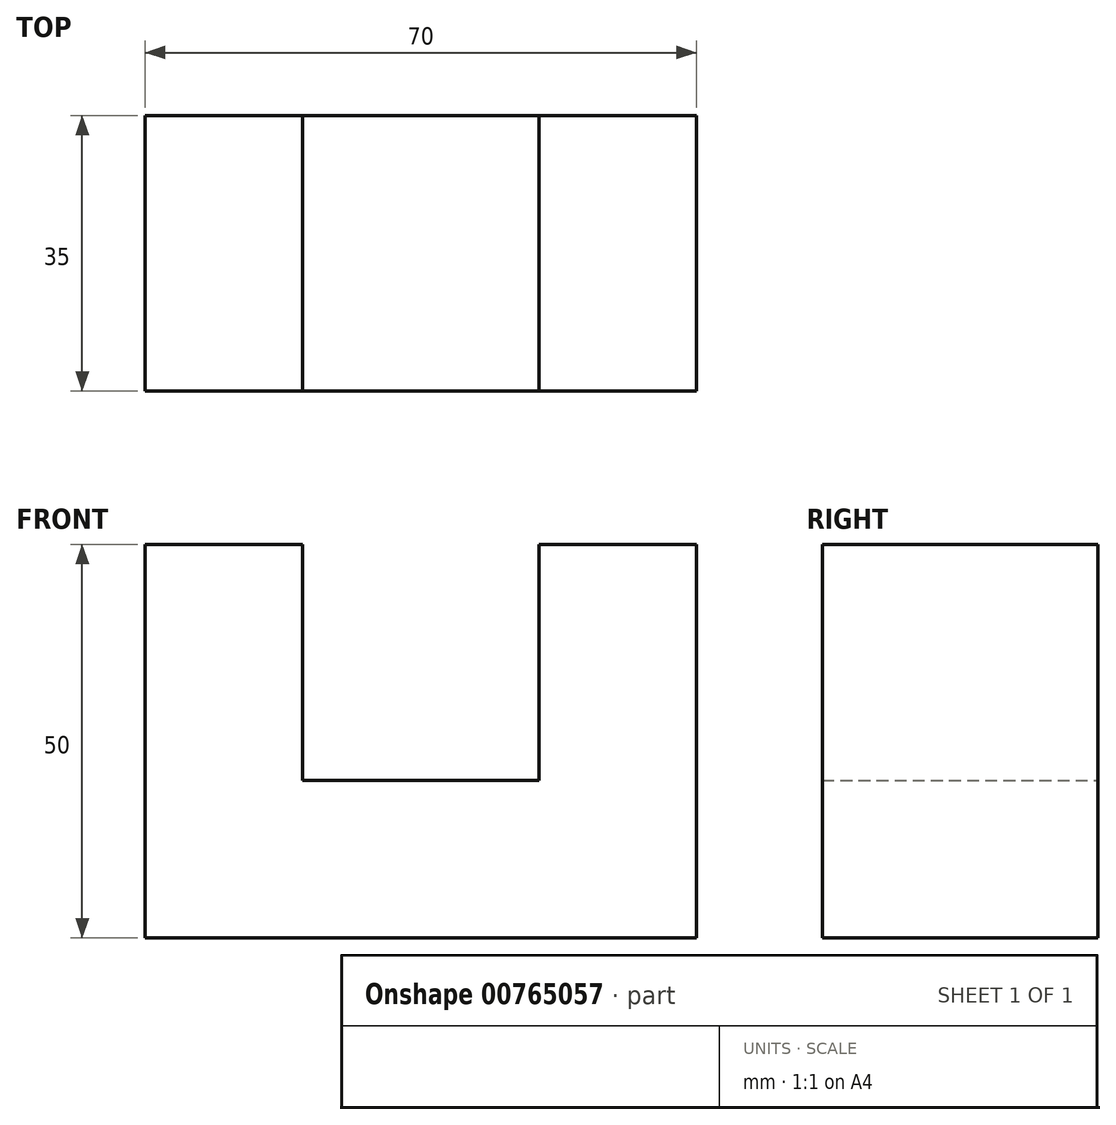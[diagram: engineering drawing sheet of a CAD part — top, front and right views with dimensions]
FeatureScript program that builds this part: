
annotation { "Feature Type Name" : "Feature", "Feature Type Description" : "" }
export const myFeature = defineFeature(function(context is Context, id is Id, definition is map)
    precondition{}
    {
        {
            var Q0;
            Q0=qCreatedBy(makeId("Front.planeOp"),FACE);
            var sketch = newSketch(context, id + "F0", { "sketchPlane" : qUnion([Q0])});
            skLineSegment(sketch, "E0.bottom", {"start": v(-35.27, 31.8) * mm, "end": v(-15.27, 31.8) * mm});
            skLineSegment(sketch, "E0.top", {"start": v(-35.27, -18.2) * mm, "end": v(34.73, -18.2) * mm});
            skLineSegment(sketch, "E0.left", {"start": v(-35.27, 31.8) * mm, "end": v(-35.27, -18.2) * mm});
            skLineSegment(sketch, "E0.right", {"start": v(34.73, 31.8) * mm, "end": v(34.73, -18.2) * mm});
            skLineSegment(sketch, "E1", {"start": v(-15.27, 31.8) * mm, "end": v(-15.27, 1.8) * mm});
            skLineSegment(sketch, "E2", {"start": v(-15.27, 1.8) * mm, "end": v(14.73, 1.8) * mm});
            skLineSegment(sketch, "E3", {"start": v(14.73, 1.8) * mm, "end": v(14.73, 31.8) * mm});
            skLineSegment(sketch, "E4.trimOffspring", {"start": v(14.73, 31.8) * mm, "end": v(34.73, 31.8) * mm});
            skSolve(sketch);
        }
        {
            var Q0;
            Q0=makeQuery(id+"F0.imprint","IMPRINT",FACE,{"disambiguationData":[TD([[makeQuery(id+"F0.imprint","IMPRINT",EDGE,{"derivedFrom":sQuery(id+"F0.wireOp",EDGE,"E0.bottom")}),-1.0]])]});
            extrude(context, id + "F1", {"entities" : qUnion([Q0]), "depth" : 35 * mm, "offsetDistance" : 25 * mm});
        }
    });
